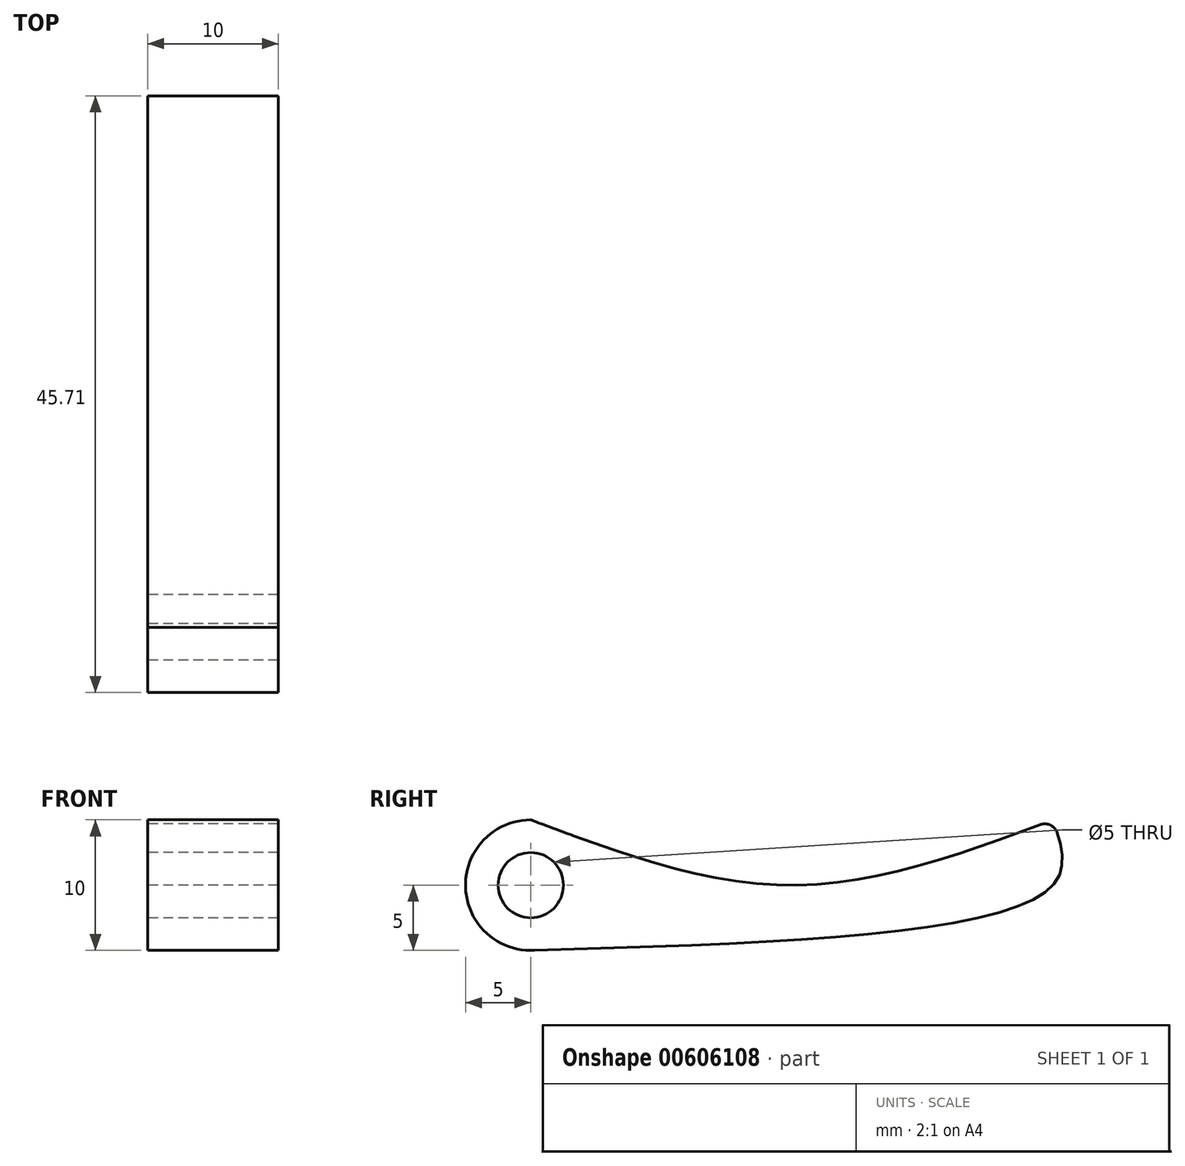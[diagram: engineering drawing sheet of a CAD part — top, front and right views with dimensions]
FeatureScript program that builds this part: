
annotation { "Feature Type Name" : "Feature", "Feature Type Description" : "" }
export const myFeature = defineFeature(function(context is Context, id is Id, definition is map)
    precondition{}
    {
        {
            var Q0;
            Q0=qCreatedBy(makeId("Right.planeOp"),FACE);
            var sketch = newSketch(context, id + "F0", { "sketchPlane" : qUnion([Q0])});
            skLineSegment(sketch, "E0.bottom", {"start": v(0, 0) * mm, "end": v(20, 0) * mm});
            skLineSegment(sketch, "E0.left", {"start": v(0, 0) * mm, "end": v(0, 10) * mm});
            skArc(sketch, "E1", {"start": v(0, 10) * mm, "mid": v(-1.74, 0.31) * mm, "end": v(3.27, 8.79) * mm});
            skCircle(sketch, "E2", {"center": v(0, 5) * mm, "radius": 2.5 * mm});
            skPoint(sketch, "E3.1.internal.snap0", {"position": v(40, 5) * mm});
            skPoint(sketch, "E3.1.internal.snap1", {"position": v(20, 0) * mm});
            skFitSpline(sketch, "E3", {"points": [v(0, 10) * mm, v(20, 5) * mm, v(40, 10) * mm], "startDerivative": vector(40, -15) * mm, "endDerivative": vector(40, 15) * mm});
            skFitSpline(sketch, "E4", {"points": [v(0, 0) * mm, v(40, 5) * mm, v(40, 10) * mm], "startDerivative": vector(74.09, 2.16) * mm, "endDerivative": vector(-7.04, 20.82) * mm});
            skPoint(sketch, "E5.orphan", {"position": v(40, 0) * mm});
            skSolve(sketch);
        }
        {
            var Q0;
            Q0 = qSketchRegion(id + "F0", true);
            extrude(context, id + "F1", {"entities" : qUnion([Q0]), "depth" : 10 * mm, "offsetDistance" : 25.4 * mm});
        }
        {
            var Q0;
            Q0=makeQuery(id+"F1.opExtrude","SWEPT_EDGE",EDGE,{"disambiguationData":[OSD([sQuery(id+"F0.wireOp",EDGE,"E3"),sQuery(id+"F0.wireOp",EDGE,"E4")])]});
            fillet(context, id + "F2", {"entities" : qUnion([Q0]), "radius" : 1 * mm, "tangentPropagation" : true, "allowEdgeOverflow" : false});
        }
    });
